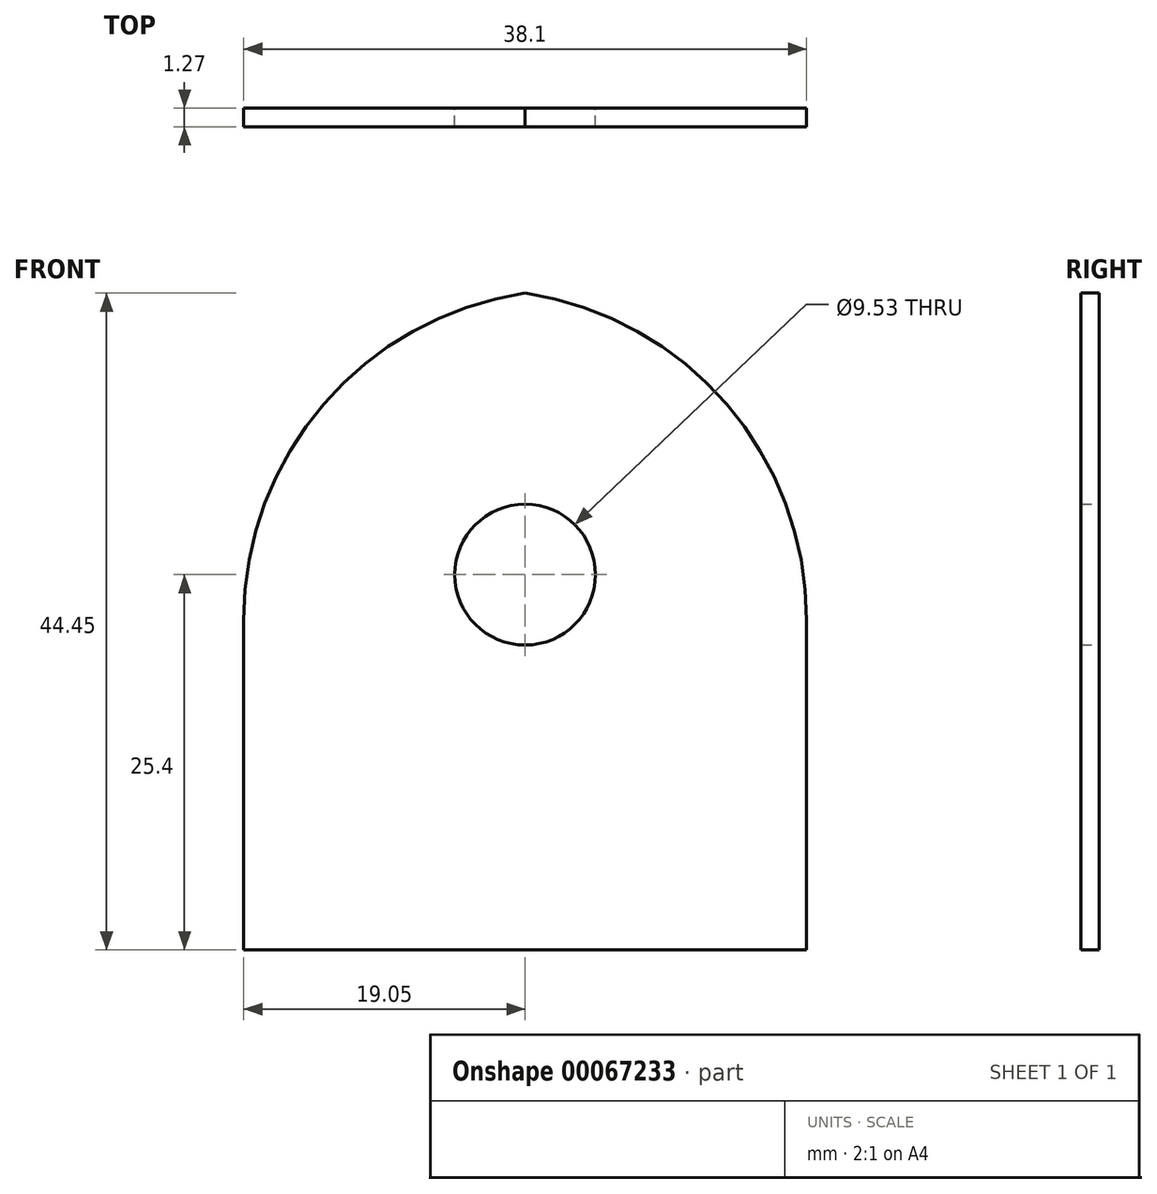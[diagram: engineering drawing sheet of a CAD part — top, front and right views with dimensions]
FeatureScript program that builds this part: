
annotation { "Feature Type Name" : "Feature", "Feature Type Description" : "" }
export const myFeature = defineFeature(function(context is Context, id is Id, definition is map)
    precondition{}
    {
        {
            var Q0;
            Q0=qCreatedBy(makeId("Front.planeOp"),FACE);
            var sketch = newSketch(context, id + "F0", { "sketchPlane" : qUnion([Q0])});
            skLineSegment(sketch, "E0", {"start": v(-19.05, 0) * mm, "end": v(-19.05, 22.35) * mm});
            skLineSegment(sketch, "E1", {"start": v(0, 44.45) * mm, "end": v(0, 30.16) * mm});
            skLineSegment(sketch, "E2", {"start": v(0, 0) * mm, "end": v(-19.05, 0) * mm});
            skArc(sketch, "E3", {"start": v(0, 30.16) * mm, "mid": v(-4.76, 25.4) * mm, "end": v(0, 20.64) * mm});
            skLineSegment(sketch, "E4.MirrorCS", {"start": v(0, 0) * mm, "end": v(19.05, 0) * mm});
            skArc(sketch, "E5.MirrorCS", {"start": v(0, 30.16) * mm, "mid": v(4.76, 25.4) * mm, "end": v(0, 20.64) * mm});
            skLineSegment(sketch, "E6.MirrorCS", {"start": v(19.05, 0) * mm, "end": v(19.05, 22.35) * mm});
            skLineSegment(sketch, "E7.trimOffspring", {"start": v(0, 25.4) * mm, "end": v(0, 0) * mm});
            skArc(sketch, "E8", {"start": v(0, 44.45) * mm, "mid": v(-13.63, 36.94) * mm, "end": v(-19.05, 22.35) * mm});
            skArc(sketch, "E9.MirrorCS", {"start": v(0, 44.45) * mm, "mid": v(13.63, 36.94) * mm, "end": v(19.05, 22.35) * mm});
            skSolve(sketch);
        }
        {
            var Q0;
            Q0=makeQuery(id+"F0.imprint","IMPRINT",FACE,{"disambiguationData":[TD([[makeQuery(id+"F0.imprint","IMPRINT",EDGE,{"derivedFrom":sQuery(id+"F0.wireOp",EDGE,"E0")}),-1.0]])]});
            var Q1;
            {var subQ1=sQuery(id+"F0.wireOp",EDGE,"E4.MirrorCS");Q1=makeQuery(id+"F0.imprint","IMPRINT",FACE,{"disambiguationData":[TD([[makeQuery(id+"F0.imprint","IMPRINT",EDGE,{"derivedFrom":subQ1}),1.0]])]});}
            extrude(context, id + "F1", {"entities" : qUnion([Q0, Q1]), "depth" : 1.27 * mm});
        }
    });
